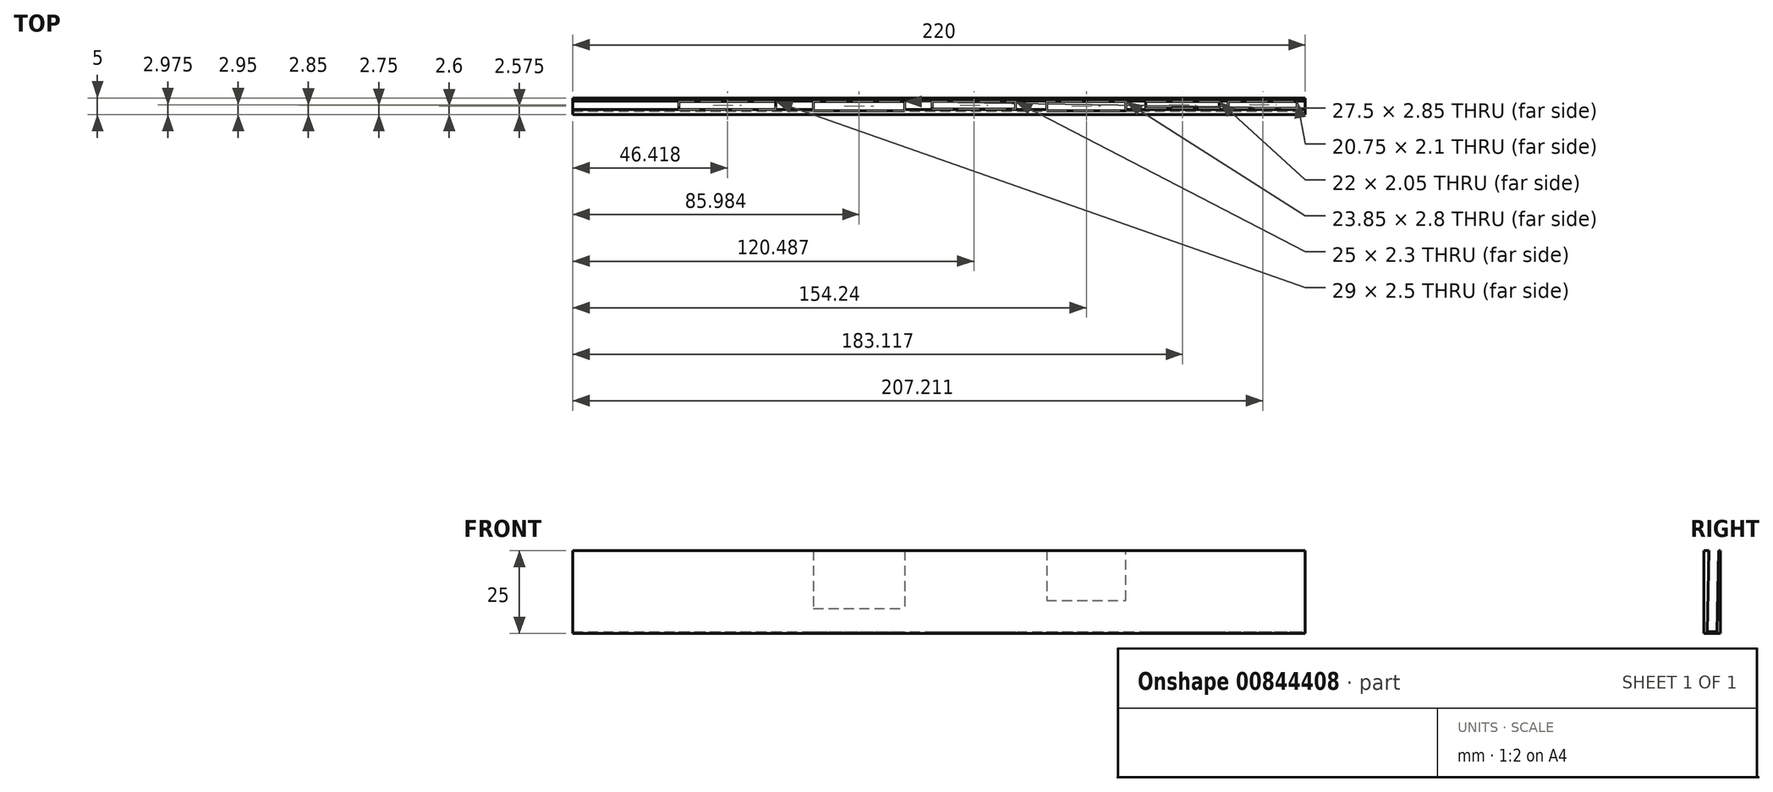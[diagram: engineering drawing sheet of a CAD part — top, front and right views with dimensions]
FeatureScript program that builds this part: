
annotation { "Feature Type Name" : "Feature", "Feature Type Description" : "" }
export const myFeature = defineFeature(function(context is Context, id is Id, definition is map)
    precondition{}
    {
        {
            var Q0;
            Q0=qCreatedBy(makeId("Top.planeOp"),FACE);
            var sketch = newSketch(context, id + "F0", { "sketchPlane" : qUnion([Q0])});
            skLineSegment(sketch, "E0.bottom", {"start": v(110, -20) * mm, "end": v(-110, -20) * mm});
            skLineSegment(sketch, "E0.top", {"start": v(110, 20) * mm, "end": v(-110, 20) * mm});
            skLineSegment(sketch, "E0.left", {"start": v(110, -20) * mm, "end": v(110, 20) * mm});
            skLineSegment(sketch, "E0.right", {"start": v(-110, -20) * mm, "end": v(-110, 20) * mm});
            skPoint(sketch, "E0.middle", {"position": v(0, 0) * mm});
            skLineSegment(sketch, "E1", {"start": v(-110, 0) * mm, "end": v(110, 0) * mm, "construction": true});
            skLineSegment(sketch, "E2.bottom", {"start": v(-49.08, 0) * mm, "end": v(-78.08, 0) * mm});
            skLineSegment(sketch, "E2.top", {"start": v(-49.08, -2.5) * mm, "end": v(-78.08, -2.5) * mm});
            skLineSegment(sketch, "E2.left", {"start": v(-49.08, 0) * mm, "end": v(-49.08, -2.5) * mm});
            skLineSegment(sketch, "E2.right", {"start": v(-78.08, 0) * mm, "end": v(-78.08, -2.5) * mm});
            skPoint(sketch, "E2.middle", {"position": v(-63.58, 0) * mm});
            skLineSegment(sketch, "E3.bottom", {"start": v(-10.27, -2.85) * mm, "end": v(-37.77, -2.85) * mm});
            skLineSegment(sketch, "E3.top", {"start": v(-10.27, 0) * mm, "end": v(-37.77, 0) * mm});
            skLineSegment(sketch, "E3.left", {"start": v(-10.27, -2.85) * mm, "end": v(-10.27, 0) * mm});
            skLineSegment(sketch, "E3.right", {"start": v(-37.77, -2.85) * mm, "end": v(-37.77, 0) * mm});
            skLineSegment(sketch, "E4.bottom", {"start": v(22.99, 0) * mm, "end": v(-2.01, 0) * mm});
            skLineSegment(sketch, "E4.top", {"start": v(22.99, -2.3) * mm, "end": v(-2.01, -2.3) * mm});
            skLineSegment(sketch, "E4.left", {"start": v(22.99, 0) * mm, "end": v(22.99, -2.3) * mm});
            skLineSegment(sketch, "E4.right", {"start": v(-2.01, 0) * mm, "end": v(-2.01, -2.3) * mm});
            skLineSegment(sketch, "E5.bottom", {"start": v(56.16, 0) * mm, "end": v(32.31, 0) * mm});
            skLineSegment(sketch, "E5.top", {"start": v(56.16, -2.8) * mm, "end": v(32.31, -2.8) * mm});
            skLineSegment(sketch, "E5.left", {"start": v(56.16, 0) * mm, "end": v(56.16, -2.8) * mm});
            skLineSegment(sketch, "E5.right", {"start": v(32.31, 0) * mm, "end": v(32.31, -2.8) * mm});
            skLineSegment(sketch, "E6.bottom", {"start": v(84.12, 0) * mm, "end": v(62.12, 0) * mm});
            skLineSegment(sketch, "E6.top", {"start": v(84.12, -2.05) * mm, "end": v(62.12, -2.05) * mm});
            skLineSegment(sketch, "E6.left", {"start": v(84.12, 0) * mm, "end": v(84.12, -2.05) * mm});
            skLineSegment(sketch, "E6.right", {"start": v(62.12, 0) * mm, "end": v(62.12, -2.05) * mm});
            skLineSegment(sketch, "E7.bottom", {"start": v(107.59, -2.1) * mm, "end": v(86.84, -2.1) * mm});
            skLineSegment(sketch, "E7.top", {"start": v(107.59, 0) * mm, "end": v(86.84, 0) * mm});
            skLineSegment(sketch, "E7.left", {"start": v(107.59, -2.1) * mm, "end": v(107.59, 0) * mm});
            skLineSegment(sketch, "E7.right", {"start": v(86.84, -2.1) * mm, "end": v(86.84, 0) * mm});
            skLineSegment(sketch, "E8.0", {"start": v(-110, 1) * mm, "end": v(110, 1) * mm});
            skLineSegment(sketch, "E9.0", {"start": v(-110, -4) * mm, "end": v(110, -4) * mm});
            skSolve(sketch);
        }
        {
            var Q0;
            Q0=makeQuery(id+"F0.imprint","IMPRINT",FACE,{"disambiguationData":[TD([[makeQuery(id+"F0.imprint","IMPRINT",EDGE,{"derivedFrom":sQuery(id+"F0.wireOp",EDGE,"E2.bottom")}),-1.0]])]});
            extrude(context, id + "F1", {"entities" : qUnion([Q0]), "depth" : 25 * mm, "offsetDistance" : 25 * mm});
        }
        {
            var Q0;
            Q0=makeQuery(id+"F1.opExtrude","SWEPT_FACE",FACE,{"disambiguationData":[OSD([sQuery(id+"F0.wireOp",EDGE,"E0.left")])]});
            var sketch = newSketch(context, id + "F2", { "sketchPlane" : qUnion([Q0])});
            skLineSegment(sketch, "E10.0", {"start": v(-4, 0) * mm, "end": v(1, 0) * mm});
            skLineSegment(sketch, "E11", {"start": v(0, 0) * mm, "end": v(1, 0) * mm, "construction": true});
            skLineSegment(sketch, "E12", {"start": v(0, 0) * mm, "end": v(-3, 0) * mm, "construction": true});
            skLineSegment(sketch, "E13", {"start": v(0.01, 0.5) * mm, "end": v(0.5, 25) * mm});
            skLineSegment(sketch, "E14", {"start": v(-2.99, 0.5) * mm, "end": v(-2.5, 25) * mm});
            skPoint(sketch, "E14.endSnap0", {"position": v(-2.5, 0) * mm});
            skLineSegment(sketch, "E15", {"start": v(1, 25) * mm, "end": v(0.5, 25) * mm, "construction": true});
            skLineSegment(sketch, "E16", {"start": v(0.5, 25) * mm, "end": v(-2.5, 25) * mm, "construction": true});
            skLineSegment(sketch, "E17.0", {"start": v(-2.99, 0.5) * mm, "end": v(0, 0.5) * mm});
            skSolve(sketch);
        }
        {
            var Q0;
            {var subQ0=sQuery(id+"F2.wireOp",EDGE,"E13");Q0=makeQuery(id+"F2.imprint","IMPRINT",FACE,{"disambiguationData":[TD([[makeQuery(id+"F2.imprint","IMPRINT",EDGE,{"derivedFrom":subQ0}),1.0]])]});}
            extrude(context, id + "F3", {"entities" : qUnion([Q0]), "operationType" : NewBodyOperationType.REMOVE, "oppositeDirection" : true, "depth" : 300 * mm, "offsetDistance" : 25 * mm});
        }
    });
